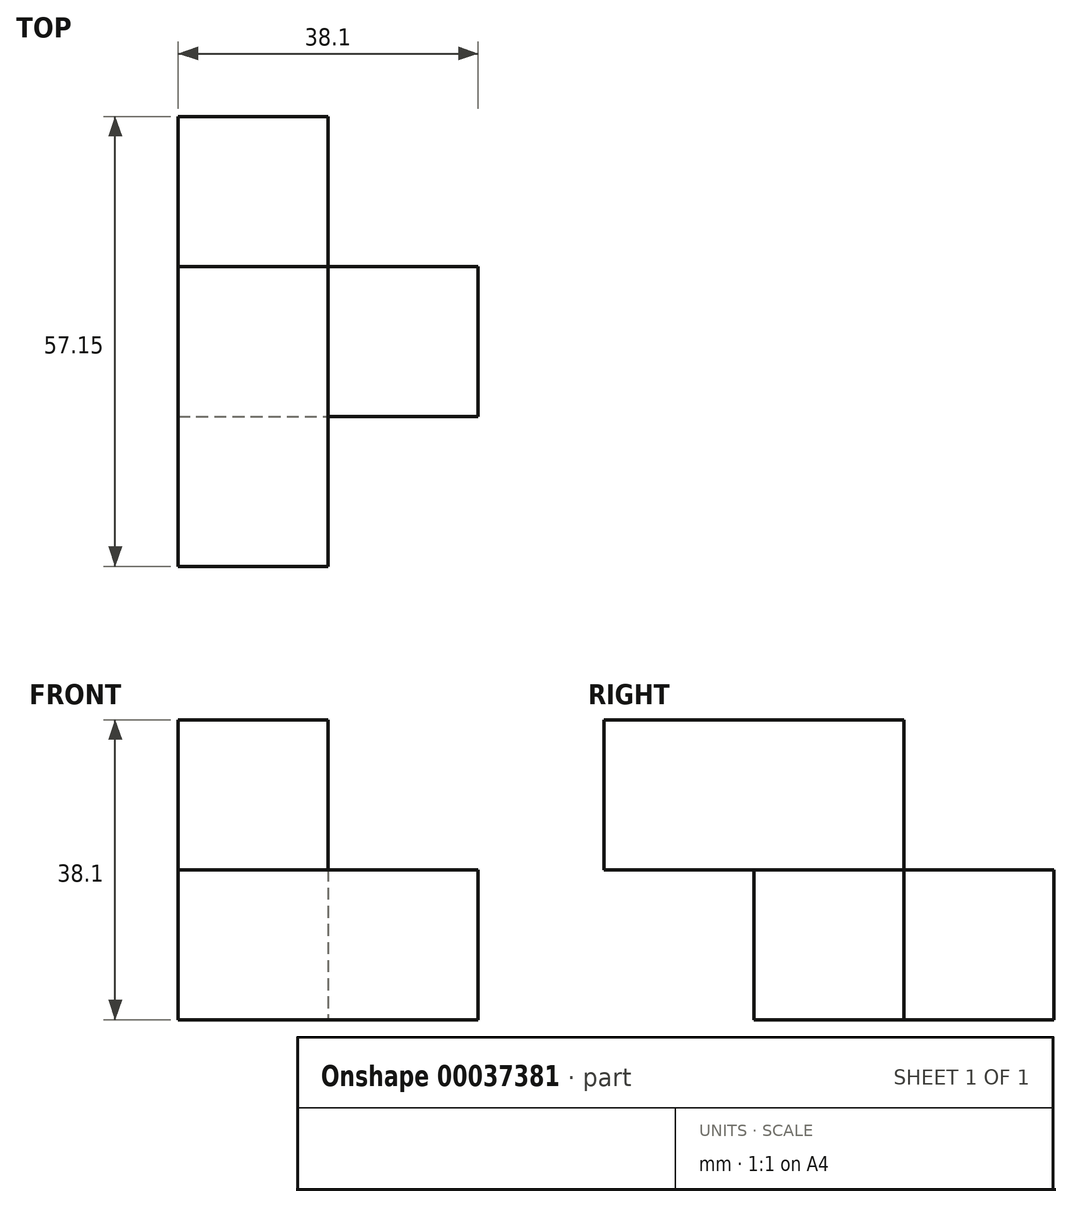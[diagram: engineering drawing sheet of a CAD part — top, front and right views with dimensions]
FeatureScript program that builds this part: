
annotation { "Feature Type Name" : "Feature", "Feature Type Description" : "" }
export const myFeature = defineFeature(function(context is Context, id is Id, definition is map)
    precondition{}
    {
        {
            var Q0;
            Q0=qCreatedBy(makeId("Top.planeOp"),FACE);
            var sketch = newSketch(context, id + "F0", { "sketchPlane" : qUnion([Q0])});
            skLineSegment(sketch, "E0.bottom", {"start": v(0, 0) * mm, "end": v(38.1, 0) * mm});
            skLineSegment(sketch, "E0.top", {"start": v(0, 57.15) * mm, "end": v(38.1, 57.15) * mm});
            skLineSegment(sketch, "E0.left", {"start": v(0, 0) * mm, "end": v(0, 57.15) * mm});
            skLineSegment(sketch, "E0.right", {"start": v(38.1, 0) * mm, "end": v(38.1, 57.15) * mm});
            skSolve(sketch);
        }
        {
            var Q0;
            Q0 = qSketchRegion(id + "F0", true);
            extrude(context, id + "F1", {"entities" : qUnion([Q0]), "depth" : 38.1 * mm});
        }
        {
            var Q0;
            Q0=makeQuery(id+"F1.opExtrude","SWEPT_FACE",FACE,{"disambiguationData":[OSD([sQuery(id+"F0.wireOp",EDGE,"E0.right")])]});
            var sketch = newSketch(context, id + "F2", { "sketchPlane" : qUnion([Q0])});
            skLineSegment(sketch, "E1.bottom", {"start": v(0, 0) * mm, "end": v(19.05, 0) * mm});
            skLineSegment(sketch, "E1.top", {"start": v(0, 19.05) * mm, "end": v(19.05, 19.05) * mm});
            skLineSegment(sketch, "E1.left", {"start": v(0, 0) * mm, "end": v(0, 19.05) * mm});
            skLineSegment(sketch, "E1.right", {"start": v(19.05, 0) * mm, "end": v(19.05, 19.05) * mm});
            skSolve(sketch);
        }
        {
            var Q0;
            Q0 = qSketchRegion(id + "F2", true);
            extrude(context, id + "F3", {"entities" : qUnion([Q0]), "operationType" : NewBodyOperationType.REMOVE, "oppositeDirection" : true, "depth" : 38.1 * mm});
        }
        {
            var Q0;
            Q0=makeQuery(id+"F1.opExtrude","SWEPT_FACE",FACE,{"disambiguationData":[OSD([sQuery(id+"F0.wireOp",EDGE,"E0.bottom")])]});
            var sketch = newSketch(context, id + "F4", { "sketchPlane" : qUnion([Q0])});
            skLineSegment(sketch, "E2.bottom", {"start": v(38.1, 19.05) * mm, "end": v(19.05, 19.05) * mm});
            skLineSegment(sketch, "E2.top", {"start": v(38.1, 38.1) * mm, "end": v(19.05, 38.1) * mm});
            skLineSegment(sketch, "E2.left", {"start": v(38.1, 19.05) * mm, "end": v(38.1, 38.1) * mm});
            skLineSegment(sketch, "E2.right", {"start": v(19.05, 19.05) * mm, "end": v(19.05, 38.1) * mm});
            skSolve(sketch);
        }
        {
            var Q0;
            Q0 = qSketchRegion(id + "F4", true);
            extrude(context, id + "F5", {"entities" : qUnion([Q0]), "operationType" : NewBodyOperationType.REMOVE, "endBound" : BoundingType.THROUGH_ALL, "oppositeDirection" : true, "depth" : 25.4 * mm});
        }
        {
            var Q0;
            Q0=makeQuery(id+"F5.boolean.opBoolean","COPY",FACE,{"derivedFrom":makeQuery(id+"F5.opExtrude","SWEPT_FACE",FACE,{"disambiguationData":[OSD([sQuery(id+"F4.wireOp",EDGE,"E2.right")])]})});
            var sketch = newSketch(context, id + "F6", { "sketchPlane" : qUnion([Q0])});
            skLineSegment(sketch, "E3.bottom", {"start": v(57.15, 19.05) * mm, "end": v(38.1, 19.05) * mm});
            skLineSegment(sketch, "E3.top", {"start": v(57.15, 38.1) * mm, "end": v(38.1, 38.1) * mm});
            skLineSegment(sketch, "E3.left", {"start": v(57.15, 19.05) * mm, "end": v(57.15, 38.1) * mm});
            skLineSegment(sketch, "E3.right", {"start": v(38.1, 19.05) * mm, "end": v(38.1, 38.1) * mm});
            skSolve(sketch);
        }
        {
            var Q0;
            Q0 = qSketchRegion(id + "F6", true);
            extrude(context, id + "F7", {"entities" : qUnion([Q0]), "operationType" : NewBodyOperationType.REMOVE, "endBound" : BoundingType.THROUGH_ALL, "oppositeDirection" : true, "depth" : 25.4 * mm});
        }
        {
            var Q0;
            Q0=makeQuery(id+"F1.opExtrude","SWEPT_FACE",FACE,{"disambiguationData":[OSD([sQuery(id+"F0.wireOp",EDGE,"E0.right")])]});
            var sketch = newSketch(context, id + "F8", { "sketchPlane" : qUnion([Q0])});
            skLineSegment(sketch, "E4.bottom", {"start": v(57.15, 0) * mm, "end": v(38.1, 0) * mm});
            skLineSegment(sketch, "E4.top", {"start": v(57.15, 19.05) * mm, "end": v(38.1, 19.05) * mm});
            skLineSegment(sketch, "E4.left", {"start": v(57.15, 0) * mm, "end": v(57.15, 19.05) * mm});
            skLineSegment(sketch, "E4.right", {"start": v(38.1, 0) * mm, "end": v(38.1, 19.05) * mm});
            skSolve(sketch);
        }
        {
            var Q0;
            Q0 = qSketchRegion(id + "F8", true);
            extrude(context, id + "F9", {"entities" : qUnion([Q0]), "operationType" : NewBodyOperationType.REMOVE, "oppositeDirection" : true, "depth" : 19.05 * mm});
        }
    });
